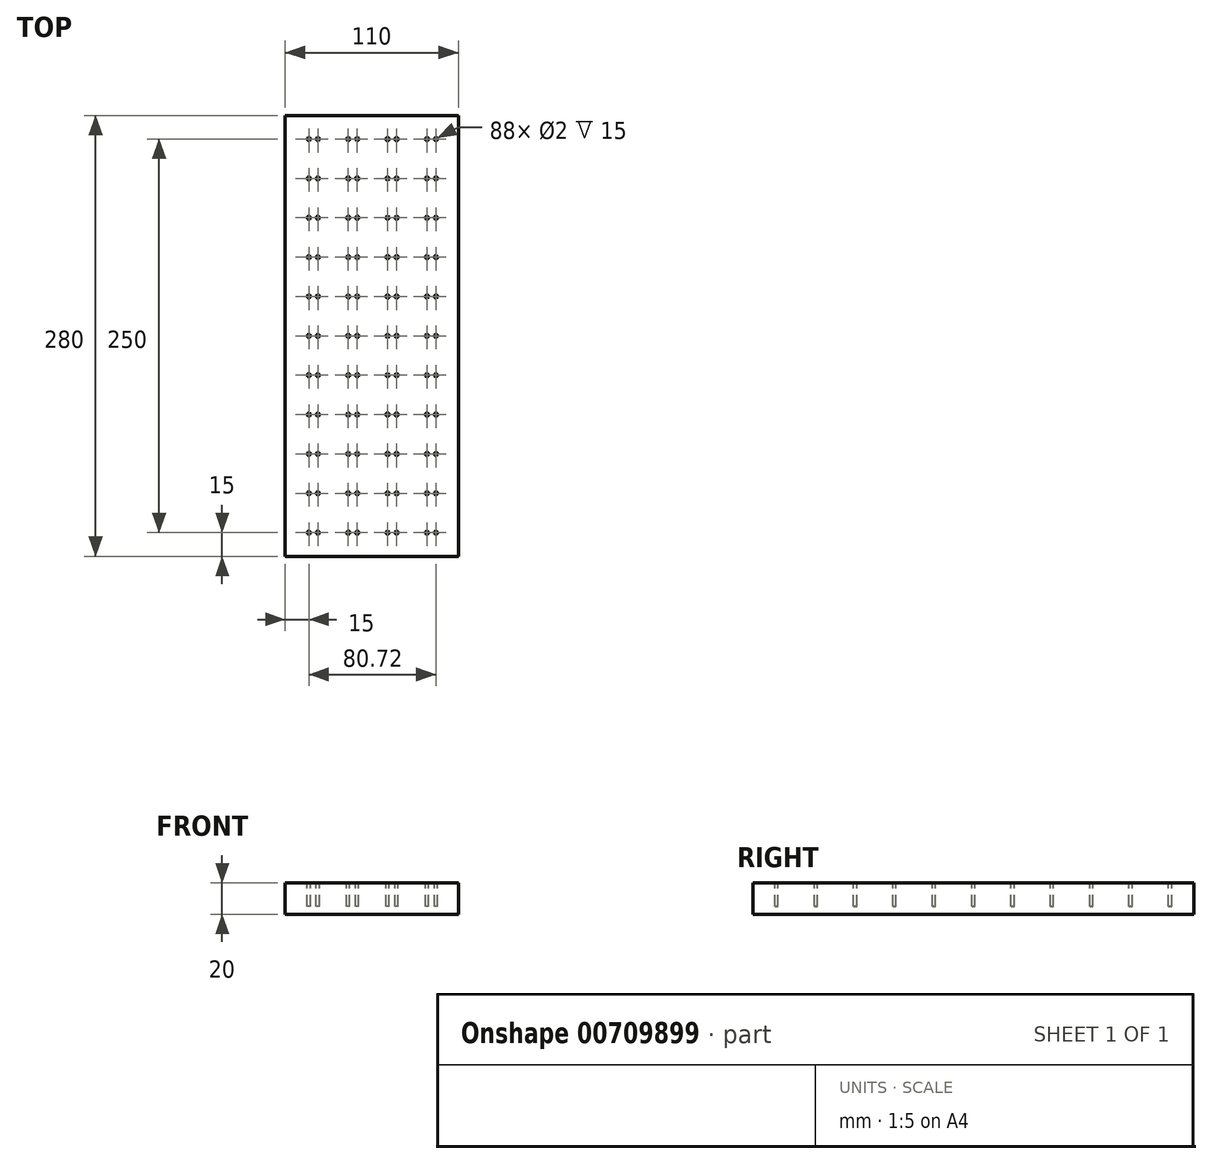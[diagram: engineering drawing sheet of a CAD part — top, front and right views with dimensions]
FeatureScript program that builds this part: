
annotation { "Feature Type Name" : "Feature", "Feature Type Description" : "" }
export const myFeature = defineFeature(function(context is Context, id is Id, definition is map)
    precondition{}
    {
        {
            var Q0;
            Q0=qCreatedBy(makeId("Top.planeOp"),FACE);
            var sketch = newSketch(context, id + "F0", { "sketchPlane" : qUnion([Q0])});
            skLineSegment(sketch, "E0.bottom", {"start": v(0, 0) * mm, "end": v(110, 0) * mm});
            skLineSegment(sketch, "E0.top", {"start": v(0, 280) * mm, "end": v(110, 280) * mm});
            skLineSegment(sketch, "E0.left", {"start": v(0, 0) * mm, "end": v(0, 280) * mm});
            skLineSegment(sketch, "E0.right", {"start": v(110, 0) * mm, "end": v(110, 280) * mm});
            skSolve(sketch);
        }
        {
            var Q0;
            Q0 = qSketchRegion(id + "F0", true);
            extrude(context, id + "F1", {"entities" : qUnion([Q0]), "depth" : 20 * mm, "offsetDistance" : 25 * mm});
        }
        {
            var Q0;
            Q0=makeQuery(id+"F1.opExtrude","CAP_FACE",FACE,{"disambiguationData":[OSD([sQuery(id+"F0.wireOp",EDGE,"E0.bottom"),sQuery(id+"F0.wireOp",EDGE,"E0.top"),sQuery(id+"F0.wireOp",EDGE,"E0.left"),sQuery(id+"F0.wireOp",EDGE,"E0.right")])],"isStart":false});
            var sketch = newSketch(context, id + "F2", { "sketchPlane" : qUnion([Q0])});
            skCircle(sketch, "E1", {"center": v(15, 15) * mm, "radius": 1 * mm});
            skCircle(sketch, "E2", {"center": v(20.72, 15) * mm, "radius": 1 * mm});
            skCircle(sketch, "E3.0.1.0", {"center": v(15, 40) * mm, "radius": 1 * mm});
            skCircle(sketch, "E3.0.1.1", {"center": v(20.72, 40) * mm, "radius": 1 * mm});
            skCircle(sketch, "E3.0.2.0", {"center": v(15, 65) * mm, "radius": 1 * mm});
            skCircle(sketch, "E3.0.2.1", {"center": v(20.72, 65) * mm, "radius": 1 * mm});
            skCircle(sketch, "E3.0.3.0", {"center": v(15, 90) * mm, "radius": 1 * mm});
            skCircle(sketch, "E3.0.3.1", {"center": v(20.72, 90) * mm, "radius": 1 * mm});
            skCircle(sketch, "E3.0.4.0", {"center": v(15, 115) * mm, "radius": 1 * mm});
            skCircle(sketch, "E3.0.4.1", {"center": v(20.72, 115) * mm, "radius": 1 * mm});
            skCircle(sketch, "E3.0.5.0", {"center": v(15, 140) * mm, "radius": 1 * mm});
            skCircle(sketch, "E3.0.5.1", {"center": v(20.72, 140) * mm, "radius": 1 * mm});
            skCircle(sketch, "E3.0.6.0", {"center": v(15, 165) * mm, "radius": 1 * mm});
            skCircle(sketch, "E3.0.6.1", {"center": v(20.72, 165) * mm, "radius": 1 * mm});
            skCircle(sketch, "E3.0.7.0", {"center": v(15, 190) * mm, "radius": 1 * mm});
            skCircle(sketch, "E3.0.7.1", {"center": v(20.72, 190) * mm, "radius": 1 * mm});
            skCircle(sketch, "E3.0.8.0", {"center": v(15, 215) * mm, "radius": 1 * mm});
            skCircle(sketch, "E3.0.8.1", {"center": v(20.72, 215) * mm, "radius": 1 * mm});
            skCircle(sketch, "E3.0.9.0", {"center": v(15, 240) * mm, "radius": 1 * mm});
            skCircle(sketch, "E3.0.9.1", {"center": v(20.72, 240) * mm, "radius": 1 * mm});
            skCircle(sketch, "E3.1.0.0", {"center": v(40, 15) * mm, "radius": 1 * mm});
            skCircle(sketch, "E3.1.0.1", {"center": v(45.72, 15) * mm, "radius": 1 * mm});
            skCircle(sketch, "E3.1.1.0", {"center": v(40, 40) * mm, "radius": 1 * mm});
            skCircle(sketch, "E3.1.1.1", {"center": v(45.72, 40) * mm, "radius": 1 * mm});
            skCircle(sketch, "E3.1.2.0", {"center": v(40, 65) * mm, "radius": 1 * mm});
            skCircle(sketch, "E3.1.2.1", {"center": v(45.72, 65) * mm, "radius": 1 * mm});
            skCircle(sketch, "E3.1.3.0", {"center": v(40, 90) * mm, "radius": 1 * mm});
            skCircle(sketch, "E3.1.3.1", {"center": v(45.72, 90) * mm, "radius": 1 * mm});
            skCircle(sketch, "E3.1.4.0", {"center": v(40, 115) * mm, "radius": 1 * mm});
            skCircle(sketch, "E3.1.4.1", {"center": v(45.72, 115) * mm, "radius": 1 * mm});
            skCircle(sketch, "E3.1.5.0", {"center": v(40, 140) * mm, "radius": 1 * mm});
            skCircle(sketch, "E3.1.5.1", {"center": v(45.72, 140) * mm, "radius": 1 * mm});
            skCircle(sketch, "E3.1.6.0", {"center": v(40, 165) * mm, "radius": 1 * mm});
            skCircle(sketch, "E3.1.6.1", {"center": v(45.72, 165) * mm, "radius": 1 * mm});
            skCircle(sketch, "E3.1.7.0", {"center": v(40, 190) * mm, "radius": 1 * mm});
            skCircle(sketch, "E3.1.7.1", {"center": v(45.72, 190) * mm, "radius": 1 * mm});
            skCircle(sketch, "E3.1.8.0", {"center": v(40, 215) * mm, "radius": 1 * mm});
            skCircle(sketch, "E3.1.8.1", {"center": v(45.72, 215) * mm, "radius": 1 * mm});
            skCircle(sketch, "E3.1.9.0", {"center": v(40, 240) * mm, "radius": 1 * mm});
            skCircle(sketch, "E3.1.9.1", {"center": v(45.72, 240) * mm, "radius": 1 * mm});
            skCircle(sketch, "E3.2.0.0", {"center": v(65, 15) * mm, "radius": 1 * mm});
            skCircle(sketch, "E3.2.0.1", {"center": v(70.72, 15) * mm, "radius": 1 * mm});
            skCircle(sketch, "E3.2.1.0", {"center": v(65, 40) * mm, "radius": 1 * mm});
            skCircle(sketch, "E3.2.1.1", {"center": v(70.72, 40) * mm, "radius": 1 * mm});
            skCircle(sketch, "E3.2.2.0", {"center": v(65, 65) * mm, "radius": 1 * mm});
            skCircle(sketch, "E3.2.2.1", {"center": v(70.72, 65) * mm, "radius": 1 * mm});
            skCircle(sketch, "E3.2.3.0", {"center": v(65, 90) * mm, "radius": 1 * mm});
            skCircle(sketch, "E3.2.3.1", {"center": v(70.72, 90) * mm, "radius": 1 * mm});
            skCircle(sketch, "E3.2.4.0", {"center": v(65, 115) * mm, "radius": 1 * mm});
            skCircle(sketch, "E3.2.4.1", {"center": v(70.72, 115) * mm, "radius": 1 * mm});
            skCircle(sketch, "E3.2.5.0", {"center": v(65, 140) * mm, "radius": 1 * mm});
            skCircle(sketch, "E3.2.5.1", {"center": v(70.72, 140) * mm, "radius": 1 * mm});
            skCircle(sketch, "E3.2.6.0", {"center": v(65, 165) * mm, "radius": 1 * mm});
            skCircle(sketch, "E3.2.6.1", {"center": v(70.72, 165) * mm, "radius": 1 * mm});
            skCircle(sketch, "E3.2.7.0", {"center": v(65, 190) * mm, "radius": 1 * mm});
            skCircle(sketch, "E3.2.7.1", {"center": v(70.72, 190) * mm, "radius": 1 * mm});
            skCircle(sketch, "E3.2.8.0", {"center": v(65, 215) * mm, "radius": 1 * mm});
            skCircle(sketch, "E3.2.8.1", {"center": v(70.72, 215) * mm, "radius": 1 * mm});
            skCircle(sketch, "E3.2.9.0", {"center": v(65, 240) * mm, "radius": 1 * mm});
            skCircle(sketch, "E3.2.9.1", {"center": v(70.72, 240) * mm, "radius": 1 * mm});
            skCircle(sketch, "E3.3.0.0", {"center": v(90, 15) * mm, "radius": 1 * mm});
            skCircle(sketch, "E3.3.0.1", {"center": v(95.72, 15) * mm, "radius": 1 * mm});
            skCircle(sketch, "E3.3.1.0", {"center": v(90, 40) * mm, "radius": 1 * mm});
            skCircle(sketch, "E3.3.1.1", {"center": v(95.72, 40) * mm, "radius": 1 * mm});
            skCircle(sketch, "E3.3.2.0", {"center": v(90, 65) * mm, "radius": 1 * mm});
            skCircle(sketch, "E3.3.2.1", {"center": v(95.72, 65) * mm, "radius": 1 * mm});
            skCircle(sketch, "E3.3.3.0", {"center": v(90, 90) * mm, "radius": 1 * mm});
            skCircle(sketch, "E3.3.3.1", {"center": v(95.72, 90) * mm, "radius": 1 * mm});
            skCircle(sketch, "E3.3.4.0", {"center": v(90, 115) * mm, "radius": 1 * mm});
            skCircle(sketch, "E3.3.4.1", {"center": v(95.72, 115) * mm, "radius": 1 * mm});
            skCircle(sketch, "E3.3.5.0", {"center": v(90, 140) * mm, "radius": 1 * mm});
            skCircle(sketch, "E3.3.5.1", {"center": v(95.72, 140) * mm, "radius": 1 * mm});
            skCircle(sketch, "E3.3.6.0", {"center": v(90, 165) * mm, "radius": 1 * mm});
            skCircle(sketch, "E3.3.6.1", {"center": v(95.72, 165) * mm, "radius": 1 * mm});
            skCircle(sketch, "E3.3.7.0", {"center": v(90, 190) * mm, "radius": 1 * mm});
            skCircle(sketch, "E3.3.7.1", {"center": v(95.72, 190) * mm, "radius": 1 * mm});
            skCircle(sketch, "E3.3.8.0", {"center": v(90, 215) * mm, "radius": 1 * mm});
            skCircle(sketch, "E3.3.8.1", {"center": v(95.72, 215) * mm, "radius": 1 * mm});
            skCircle(sketch, "E3.3.9.0", {"center": v(90, 240) * mm, "radius": 1 * mm});
            skCircle(sketch, "E3.3.9.1", {"center": v(95.72, 240) * mm, "radius": 1 * mm});
            skLineSegment(sketch, "E3.direction1", {"start": v(10, 10) * mm, "end": v(35, 10) * mm, "construction": true});
            skLineSegment(sketch, "E3.direction2", {"start": v(10, 10) * mm, "end": v(10, 35) * mm, "construction": true});
            skCircle(sketch, "E4.0.0.10", {"center": v(15, 265) * mm, "radius": 1 * mm});
            skCircle(sketch, "E4.2.0.10", {"center": v(20.72, 265) * mm, "radius": 1 * mm});
            skCircle(sketch, "E4.0.1.10", {"center": v(40, 265) * mm, "radius": 1 * mm});
            skCircle(sketch, "E4.2.1.10", {"center": v(45.72, 265) * mm, "radius": 1 * mm});
            skCircle(sketch, "E4.0.2.10", {"center": v(65, 265) * mm, "radius": 1 * mm});
            skCircle(sketch, "E4.2.2.10", {"center": v(70.72, 265) * mm, "radius": 1 * mm});
            skCircle(sketch, "E4.0.3.10", {"center": v(90, 265) * mm, "radius": 1 * mm});
            skCircle(sketch, "E4.2.3.10", {"center": v(95.72, 265) * mm, "radius": 1 * mm});
            skSolve(sketch);
        }
        {
            var Q0;
            Q0 = qSketchRegion(id + "F2", true);
            extrude(context, id + "F3", {"entities" : qUnion([Q0]), "operationType" : NewBodyOperationType.REMOVE, "oppositeDirection" : true, "depth" : 15 * mm, "offsetDistance" : 25 * mm});
        }
    });
